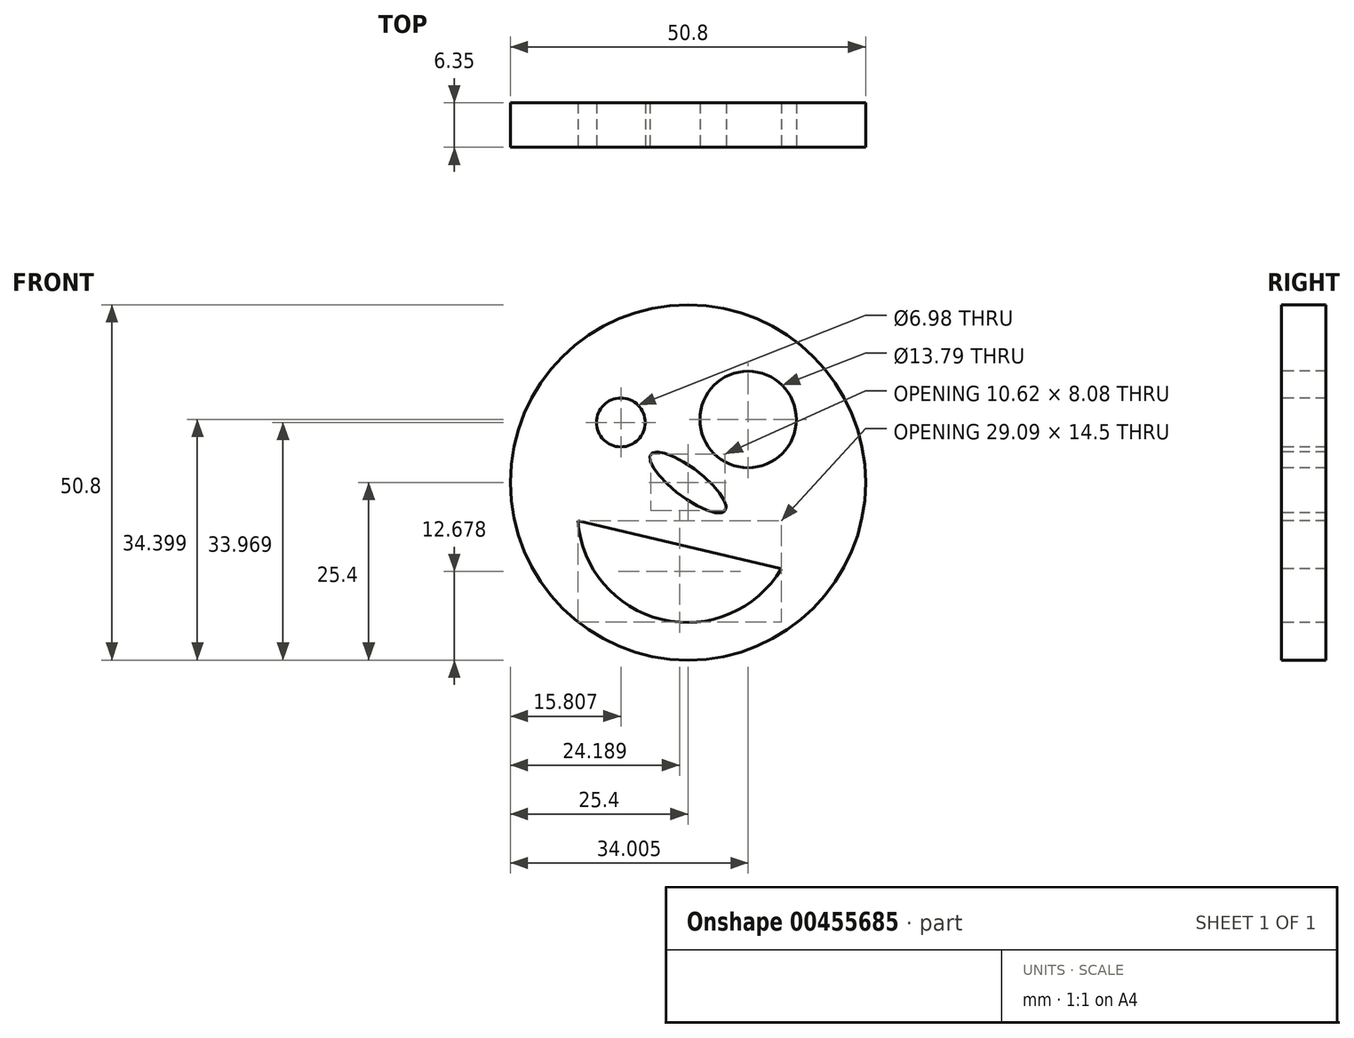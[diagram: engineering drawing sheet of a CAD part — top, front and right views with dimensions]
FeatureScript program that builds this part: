
annotation { "Feature Type Name" : "Feature", "Feature Type Description" : "" }
export const myFeature = defineFeature(function(context is Context, id is Id, definition is map)
    precondition{}
    {
        {
            var Q0;
            Q0=qCreatedBy(makeId("Front.planeOp"),FACE);
            var sketch = newSketch(context, id + "F0", { "sketchPlane" : qUnion([Q0])});
            skCircle(sketch, "E0", {"center": v(0, 0) * mm, "radius": 25.4 * mm});
            skSolve(sketch);
        }
        {
            var Q0;
            Q0 = qSketchRegion(id + "F0", true);
            extrude(context, id + "F1", {"entities" : qUnion([Q0]), "depth" : 6.35 * mm});
        }
        {
            var Q0;
            Q0=makeQuery(id+"F1.opExtrude","CAP_FACE",FACE,{"disambiguationData":[OSD([sQuery(id+"F0.wireOp",EDGE,"E0")])],"isStart":false});
            var sketch = newSketch(context, id + "F2", { "sketchPlane" : qUnion([Q0])});
            skCircle(sketch, "E1", {"center": v(-9.6, 8.57) * mm, "radius": 3.49 * mm});
            skCircle(sketch, "E2", {"center": v(8.6, 9) * mm, "radius": 6.9 * mm});
            skEllipse(sketch, "E3", {"center": v(0, 0) * mm, "majorRadius": 6.67 * mm, "minorRadius": 2.1 * mm, "majorAxis": v(0.8, -0.6)});
            skArc(sketch, "E4", {"start": v(-15.76, -5.47) * mm, "mid": v(-3.74, -19.6) * mm, "end": v(13.33, -12.35) * mm});
            skLineSegment(sketch, "E5", {"start": v(-15.76, -5.47) * mm, "end": v(13.33, -12.35) * mm});
            skSolve(sketch);
        }
        {
            var Q0;
            Q0 = qSketchRegion(id + "F2", true);
            extrude(context, id + "F3", {"entities" : qUnion([Q0]), "operationType" : NewBodyOperationType.REMOVE, "oppositeDirection" : true, "depth" : 6.35 * mm});
        }
    });
